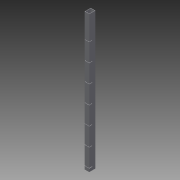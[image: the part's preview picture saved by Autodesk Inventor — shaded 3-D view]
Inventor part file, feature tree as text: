
AUTODESK INVENTOR PART (.ipt)
format: ipt  version: 2013 (Build 170138000, 138)  size: 139,776 bytes
history: native  units: in
note: dims shown in document units (in); Inventor stores cm internally (conversion verified against a paired STEP export)
features: other x4, extrude x1, sketch x1
ambient origin geometry x8: Origin, YZ Plane, XZ Plane, XY Plane, X Axis, Y Axis, Z Axis, Center Point
bodies: Solid1 (feature_tree)
feature tree (6):
  other  "Table"
  other  "squareTube1.5x2.ipt"
  extrude  "Extrusion2"  TaperAngle=0.0deg  [1 undecoded]
  other  "Solid1::squareTube1.5x2.ipt"
  other  "TaggingFeature1"
  sketch  "Sketch2"  dims[d0=1.5in d1=2.0in d2=0.125in d4=0.0in d20=2.7559in d22=6.0in d23=0.3937in d25=1.0in d27=1.0in d28=0.0in d29=0.1875in d30=1.0in]
note: 1 required parameter value undecoded (feature->parameter linkage not recoverable at this tier; creation-order binding heuristic only, values carry confidence <= 0.55)
